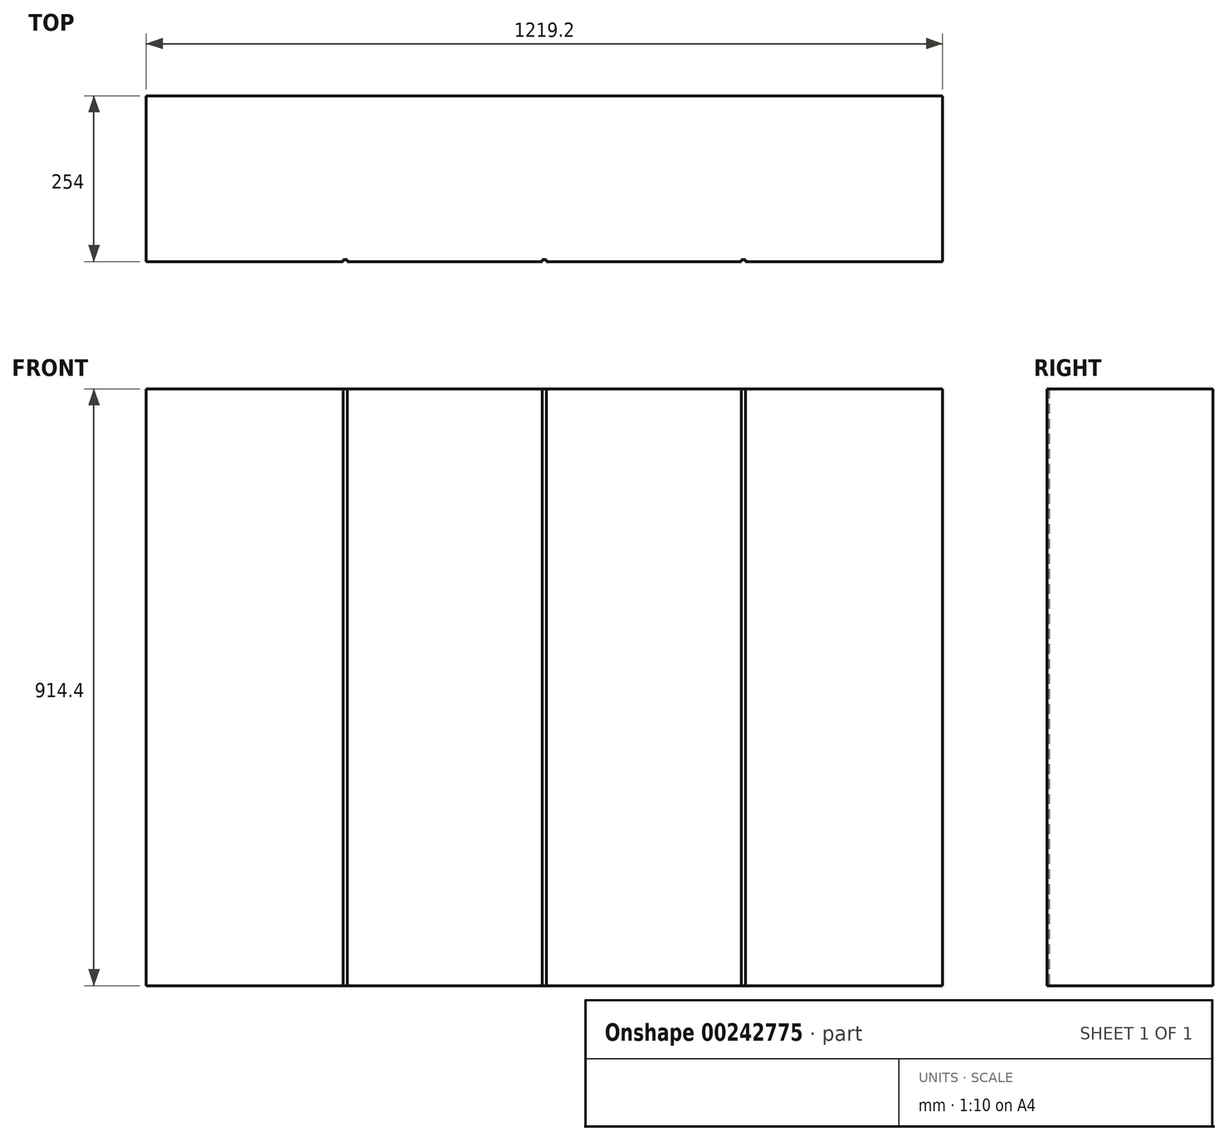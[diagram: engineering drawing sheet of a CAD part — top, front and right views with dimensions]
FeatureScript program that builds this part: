
annotation { "Feature Type Name" : "Feature", "Feature Type Description" : "" }
export const myFeature = defineFeature(function(context is Context, id is Id, definition is map)
    precondition{}
    {
        {
            var Q0;
            Q0=qCreatedBy(makeId("Top.planeOp"),FACE);
            var sketch = newSketch(context, id + "F0", { "sketchPlane" : qUnion([Q0])});
            skLineSegment(sketch, "E0.bottom", {"start": v(0, 0) * mm, "end": v(1219.2, 0) * mm});
            skLineSegment(sketch, "E0.top", {"start": v(0, -254) * mm, "end": v(1219.2, -254) * mm});
            skLineSegment(sketch, "E0.left", {"start": v(0, 0) * mm, "end": v(0, -254) * mm});
            skLineSegment(sketch, "E0.right", {"start": v(1219.2, 0) * mm, "end": v(1219.2, -254) * mm});
            skSolve(sketch);
        }
        {
            var Q0;
            Q0=makeQuery(id+"F0.imprint","IMPRINT",FACE,{"disambiguationData":[TD([[makeQuery(id+"F0.imprint","IMPRINT",EDGE,{"derivedFrom":sQuery(id+"F0.wireOp",EDGE,"E0.bottom")}),-1.0]])]});
            extrude(context, id + "F1", {"entities" : qUnion([Q0]), "depth" : 914.4 * mm});
        }
        {
            var Q0;
            Q0=makeQuery(id+"F1.opExtrude","SWEPT_FACE",FACE,{"disambiguationData":[OSD([sQuery(id+"F0.wireOp",EDGE,"E0.top")])]});
            var sketch = newSketch(context, id + "F2", { "sketchPlane" : qUnion([Q0])});
            skLineSegment(sketch, "E1.bottom", {"start": v(606.43, 914.4) * mm, "end": v(612.78, 914.4) * mm});
            skLineSegment(sketch, "E1.top", {"start": v(606.43, 0) * mm, "end": v(612.78, 0) * mm});
            skLineSegment(sketch, "E1.left", {"start": v(606.43, 914.4) * mm, "end": v(606.43, 0) * mm});
            skLineSegment(sketch, "E1.right", {"start": v(612.78, 914.4) * mm, "end": v(612.78, 0) * mm});
            skLineSegment(sketch, "E2", {"start": v(609.6, 914.4) * mm, "end": v(609.6, 0) * mm, "construction": true});
            skLineSegment(sketch, "E3.bottom", {"start": v(911.23, 914.4) * mm, "end": v(917.58, 914.4) * mm});
            skLineSegment(sketch, "E3.top", {"start": v(911.22, 0) * mm, "end": v(917.58, 0) * mm});
            skLineSegment(sketch, "E3.left", {"start": v(911.23, 914.4) * mm, "end": v(911.22, 0) * mm});
            skLineSegment(sketch, "E3.right", {"start": v(917.58, 914.4) * mm, "end": v(917.57, 0) * mm});
            skLineSegment(sketch, "E4.bottom", {"start": v(301.63, 914.4) * mm, "end": v(307.97, 914.4) * mm});
            skLineSegment(sketch, "E4.top", {"start": v(301.62, 0) * mm, "end": v(307.98, 0) * mm});
            skLineSegment(sketch, "E4.left", {"start": v(301.63, 914.4) * mm, "end": v(301.62, 0) * mm});
            skLineSegment(sketch, "E4.right", {"start": v(307.98, 914.4) * mm, "end": v(307.97, 0) * mm});
            skLineSegment(sketch, "E5", {"start": v(0, 0) * mm, "end": v(609.6, 0) * mm, "construction": true});
            skLineSegment(sketch, "E6", {"start": v(304.8, 0) * mm, "end": v(304.8, 914.4) * mm, "construction": true});
            skLineSegment(sketch, "E7", {"start": v(609.6, 0) * mm, "end": v(1219.2, 0) * mm, "construction": true});
            skLineSegment(sketch, "E8", {"start": v(914.4, 0) * mm, "end": v(914.4, 914.4) * mm, "construction": true});
            skSolve(sketch);
        }
        {
            var Q0;
            Q0 = qSketchRegion(id + "F2", true);
            extrude(context, id + "F3", {"entities" : qUnion([Q0]), "operationType" : NewBodyOperationType.REMOVE, "oppositeDirection" : true, "depth" : 3.17 * mm});
        }
    });
